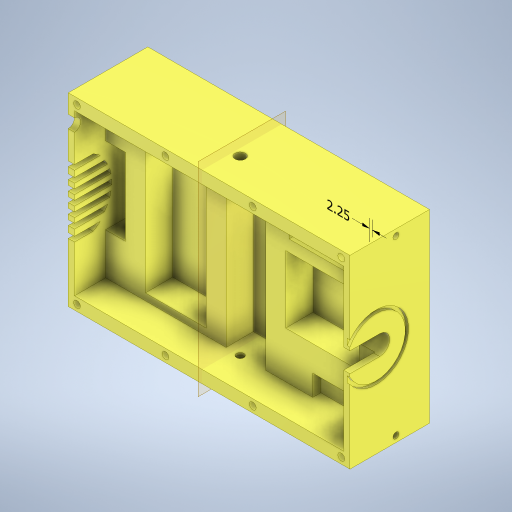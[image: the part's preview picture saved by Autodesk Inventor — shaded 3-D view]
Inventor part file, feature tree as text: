
AUTODESK INVENTOR PART (.ipt)
format: ipt  version: 2023 (Build 270158030, 158C)  size: 717,824 bytes
history: native  units: mm
features: sketch x17, extrude x16, projected_geometry x6, hole x4, other x2, mirror x1, plane x1
ambient origin geometry x8: Origin, YZ Plane, XZ Plane, XY Plane, X Axis, Y Axis, Z Axis, Center Point
bodies: Solid1 (feature_tree)
feature tree (47):
  other  "Annotations"
  extrude  "MainInnerBodyExtrusion"  Depth=149.0mm
  extrude  "HoleForCamerabase"  Depth=50.0mm
  extrude  "HoleForFan"  Depth=59.0mm
  extrude  "HoleForPi"  TaperAngle=0.0deg  [1 undecoded]
  extrude  "HoleForPoeAdapter"  Depth=62.0mm
  extrude  "HoleForThermister"  Depth=47.0mm
  extrude  "HoleForSensor"  Depth=32.0mm
  extrude  "SlotsForRearFan"  Depth=47.0mm
  extrude  "VentForCamera"  Depth=16.0mm
  extrude  "HoleForLens"  Depth=118.0mm
  sketch  "Sketch23"  dims[d26=49.0mm d27=118.0mm]
  hole  "Hole for 6-32 Insert"  [1 undecoded]
  hole  "Screw hole for 6-32 screw"  [1 undecoded]
  hole  "Side hole for 1-4 20 insert"  [1 undecoded]
  mirror  "Mirror for side insert"
  extrude  "Extrusion18"  Depth=17.0mm
  extrude  "HoleForPowerWire"  TaperAngle=0.0deg  [1 undecoded]
  extrude  "Extrusion22"  Depth=2.0mm
  extrude  "Extrusion23"  Depth=4.0mm
  extrude  "ExtrusionForBottom"  Depth=4.0mm
  extrude  "CutOutForFilter"  Depth=4.0mm
  hole  "Hole13"  [1 undecoded]
  plane  "Work Plane6"
  sketch  "Sketch1"  dims[d0=222.7mm d1=149.0mm]
  sketch  "Sketch3"  dims[d2=50.0mm d3=0.0mm d5=15.7mm]
  sketch  "Sketch4"  dims[d6=54.0mm d7=59.0mm]
  sketch  "Sketch6"  dims[d8=47.0mm d9=0.0mm]
  sketch  "Sketch7"  dims[d13=16.0mm d14=62.0mm]
  sketch  "Sketch11"  dims[d15=3.0mm d16=47.0mm]
  sketch  "Sketch15"  dims[d17=0.0mm d20=32.0mm]
  sketch  "Sketch16"  dims[d21=129.0mm d22=47.0mm]
  sketch  "Sketch18"  dims[d23=0.0mm d25=16.0mm]
  sketch  "Sketch24"  dims[d28=47.0mm d29=0.0mm]
  sketch  "Sketch25"  dims[d36=69.0mm d37=28.0mm]
  projected_geometry  "Projected Loop1"
  sketch  "Sketch26"  dims[d38=47.0mm d39=0.0mm]
  sketch  "Sketch37"  dims[d42=50.0mm d43=17.0mm]
  projected_geometry  "Projected Loop3"
  projected_geometry  "Projected Loop4"
  sketch  "Sketch39"  dims[d46=31.5mm d47=0.0mm]
  projected_geometry  "Projected Loop5"
  sketch  "Sketch43"  dims[d67=60.0mm d69=2.0mm]
  projected_geometry  "Projected Loop8"
  sketch  "Sketch47"  dims[d71=4.0mm d72=4.0mm d73=4.0mm d75=4.0mm d76=10.0mm d77=0.0mm d78=15.5mm d79=22.0mm d85=3.0mm d86=3.0mm d87=10.0mm d88=16.0mm d89=1.5mm d90=3.0mm d91=3.0mm d92=3.0mm d93=0.0mm d94=0.0mm d95=15.0mm d97=16.0mm d98=10.0mm d99=0.0mm d106=5.0mm d108=5.0mm d109=4.7mm d110=6.0mm d111=5.54mm d112=5.55mm d113=90.0deg d114=7.2mm d115=20.594885mm d116=3.797mm d117=6.0mm d118=12.7mm d119=2.362mm d120=90.0deg d121=15.0mm d122=20.594885mm d130=7.666mm d131=6.0mm d132=8.406mm d133=7.41mm d134=90.0deg d135=9.53mm d136=20.594885mm d137=24.0mm d138=10.0mm d139=3.0mm d140=25.0mm d141=0.0mm d142=30.0mm d144=10.0mm d145=0.0mm d222=76.2mm d223=76.2mm d224=76.2mm d225=76.2mm d226=25.0mm d227=111.350057mm d228=2.0mm d229=0.0mm d230=2.0mm d231=0.0mm d232=14.0mm d233=0.0mm d255=21.0mm d256=52.25mm d257=47.0mm d258=2.25mm d259=0.0mm d293=27.0mm d294=5.0mm d295=5.0mm d296=4.699mm d297=6.0mm d298=4.8514mm d299=5.55244mm d300=90.0deg d301=7.1374mm d302=0.0mm d333=2.807045mm d334=7.557548mm d335=2.25mm]
  projected_geometry  "Projected Loop12"
  other  "Linear Dimension 1"
note: 6 required parameter values undecoded (feature->parameter linkage not recoverable at this tier; creation-order binding heuristic only, values carry confidence <= 0.55)
